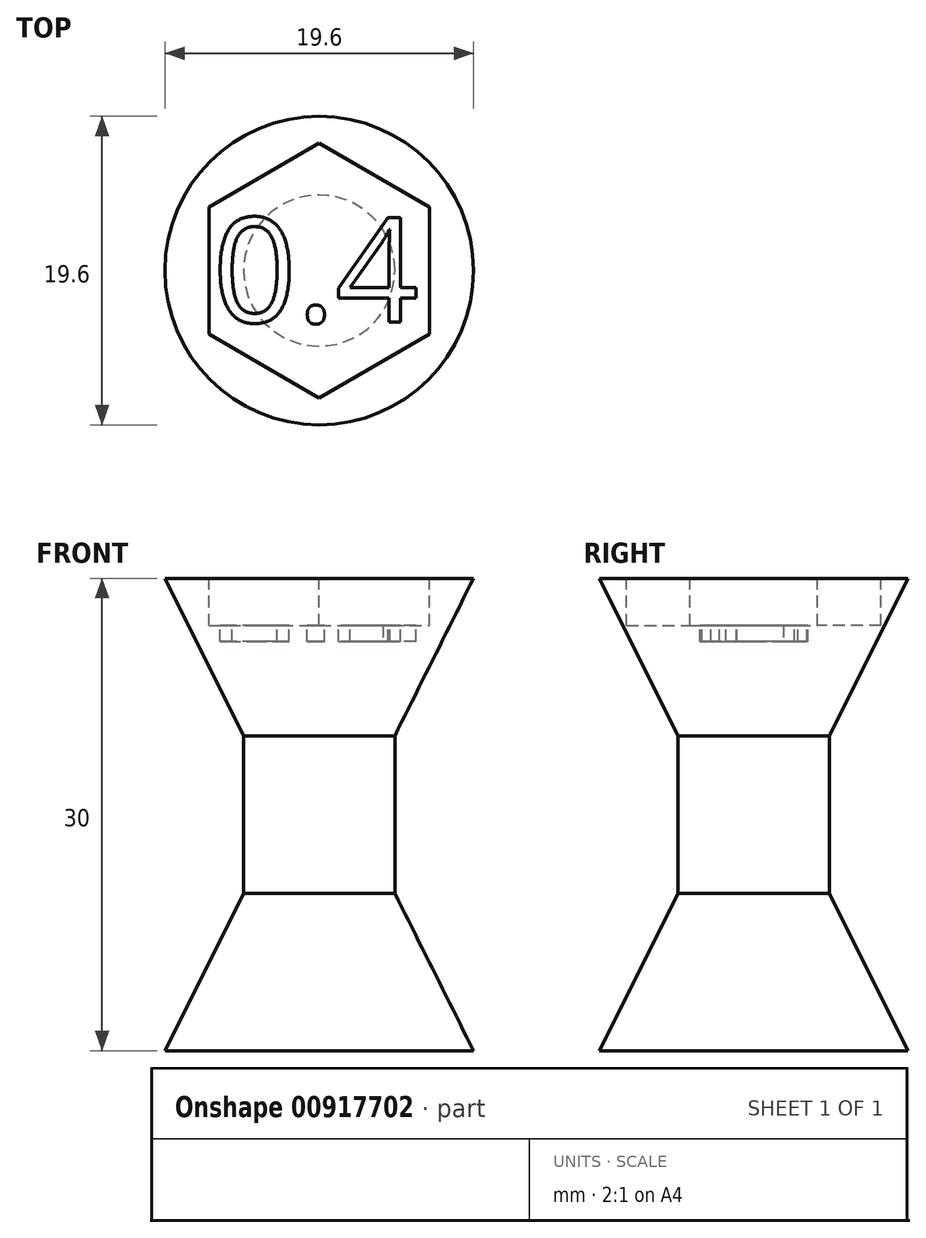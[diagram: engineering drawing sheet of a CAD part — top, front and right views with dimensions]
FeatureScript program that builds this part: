
annotation { "Feature Type Name" : "Feature", "Feature Type Description" : "" }
export const myFeature = defineFeature(function(context is Context, id is Id, definition is map)
    precondition{}
    {
        {
            var Q0;
            Q0=qCreatedBy(makeId("Front.planeOp"),FACE);
            var sketch = newSketch(context, id + "F0", { "sketchPlane" : qUnion([Q0])});
            skLineSegment(sketch, "E0", {"start": v(0, 15) * mm, "end": v(0, -15) * mm});
            skLineSegment(sketch, "E1", {"start": v(0, -15) * mm, "end": v(9.8, -15) * mm});
            skLineSegment(sketch, "E2", {"start": v(9.8, -15) * mm, "end": v(4.8, -5) * mm});
            skLineSegment(sketch, "E3", {"start": v(4.8, -5) * mm, "end": v(4.8, 5) * mm});
            skLineSegment(sketch, "E4", {"start": v(4.8, 5) * mm, "end": v(9.8, 15) * mm});
            skLineSegment(sketch, "E5", {"start": v(9.8, 15) * mm, "end": v(0, 15) * mm});
            skSolve(sketch);
        }
        {
            var Q0;
            Q0=qSketchRegion(id+"F0",true);
            var Q1;
            Q1=sQuery(id+"F0.wireOp",EDGE,"E0");
            revolve(context, id + "F1", {"surfaceOperationType" : NewSurfaceOperationType.NEW, "entities" : qUnion([Q0]), "axis" : qUnion([Q1]), "revolveType" : RevolveType.FULL});
        }
        {
            var Q0;
            Q0=makeQuery(id+"F1.opRevolve","SWEPT_FACE",FACE,{"disambiguationData":[OSD([sQuery(id+"F0.wireOp",EDGE,"E5")])]});
            var sketch = newSketch(context, id + "F2", { "sketchPlane" : qUnion([Q0])});
            skCircle(sketch, "E6.cCircle", {"center": v(0, 0) * mm, "radius": 7 * mm, "construction": true});
            skLineSegment(sketch, "E6.0", {"start": v(0, 8.08) * mm, "end": v(7, 4.04) * mm});
            skLineSegment(sketch, "E6.1", {"start": v(7, 4.04) * mm, "end": v(7, -4.04) * mm});
            skLineSegment(sketch, "E6.2", {"start": v(7, -4.04) * mm, "end": v(0, -8.08) * mm});
            skLineSegment(sketch, "E6.3", {"start": v(0, -8.08) * mm, "end": v(-7, -4.04) * mm});
            skLineSegment(sketch, "E6.4", {"start": v(-7, -4.04) * mm, "end": v(-7, 4.04) * mm});
            skLineSegment(sketch, "E6.5", {"start": v(-7, 4.04) * mm, "end": v(0, 8.08) * mm});
            skPoint(sketch, "E6.0.midPoint", {"position": v(3.5, 6.06) * mm});
            skSolve(sketch);
        }
        {
            var Q0;
            Q0=qSketchRegion(id+"F2",true);
            extrude(context, id + "F3", {"entities" : qUnion([Q0]), "operationType" : NewBodyOperationType.REMOVE, "oppositeDirection" : true, "depth" : 3 * mm, "offsetDistance" : 25 * mm});
        }
        {
            var Q0;
            Q0=makeQuery(id+"F3.boolean.opBoolean","COPY",FACE,{"derivedFrom":makeQuery(id+"F3.opExtrude","CAP_FACE",FACE,{"disambiguationData":[OSD([sQuery(id+"F2.wireOp",EDGE,"E6.0"),sQuery(id+"F2.wireOp",EDGE,"E6.1"),sQuery(id+"F2.wireOp",EDGE,"E6.2"),sQuery(id+"F2.wireOp",EDGE,"E6.3"),sQuery(id+"F2.wireOp",EDGE,"E6.4"),sQuery(id+"F2.wireOp",EDGE,"E6.5")])],"isStart":false})});
            var sketch = newSketch(context, id + "F4", { "sketchPlane" : qUnion([Q0])});
            skText(sketch, "E7", { "text": "0.4", "fontName": "OpenSans-Regular.ttf"});
            const initialGuessF4  = {"E7": [-0.00675, -0.00328, 1, 0, 0.00668]};
            skSetInitialGuess(sketch, initialGuessF4);
            skSolve(sketch);
        }
        {
            var Q0;
            Q0=qSketchRegion(id+"F4",true);
            extrude(context, id + "F5", {"entities" : qUnion([Q0]), "operationType" : NewBodyOperationType.REMOVE, "oppositeDirection" : true, "depth" : 1 * mm, "offsetDistance" : 25 * mm});
        }
    });
